# Revit family: ESTS
name_source: partatom
category: Mechanical Equipment
revit_build: Autodesk Revit 2018 (Build: 20170223_1515(x64)
units: mm (PartAtom-declared; Revit-internal decimal feet)

## family parameters
Always vertical = Yes
Cut with Voids When Loaded = No
Part Type = Normal
Room Calculation Point = No
Round Connector Dimension = Use Radius
Shared = No
Work Plane-Based = No

## types (92) — shared parameters
Description = Series Fan Powered Air Terminal with ECM Motor
Discharge Offset = 3"
Filter = 1"
Induction Offset = 1 1/8"
Inlet S = 5 1/2"
Manufacturer = Anemostat
Model = ESTS
URL = http://www.anemostat.com

## per-type parameters (varying)
| type | Diameter | Discharge Height "Y" | Discharge Width "X" | Duct Inlet | ELBOW LEFT | ELBOW RIGHT | Height | Induction Width "C" | Inlet Offset | Inlet Right | Left | Length | Q5A | Q5B | Q5Q | Radius | Right | Width |
| ESTS 3/4-hp - 07R with S/ELBOW | 6 7/8" | 16" | 19" | 3" | No | Yes | 20" | 21" | 3" | Yes | No | 48" | 20" | 24" | 20" | 3 7/16" | Yes | 48" |
| ESTS 3/4-hp - 07L with S/ELBOW | 6 7/8" | 16" | 19" | 3" | Yes | No | 20" | 21" | 4" | No | Yes | 48" | 20" | 24" | 20" | 3 7/16" | No | 48" |
| ESTS 3/4-hp - 07L W/OUT S/ELBOW | 6 7/8" | 16" | 19" | 3" | No | No | 20" | 21" | 4" | No | Yes | 48" | 20" | 24" | 20" | 3 7/16" | No | 48" |
| ESTS 3/4-hp - 07R W/OUT S/ELBOW | 6 7/8" | 16" | 19" | 3" | No | No | 20" | 21" | 3" | Yes | No | 48" | 20" | 24" | 20" | 3 7/16" | Yes | 48" |
| ESTS 1/3-hp - 10L W/OUT S/ELBOW | 9 7/8" | 11" | 11 1/2" | 5" | No | No | 18" | 12" | 4" | No | Yes | 36" | 18" | 18" | 18" | 4 15/16" | No | 32" |
| ESTS 1/3-hp - 10L with S/ELBOW | 9 7/8" | 11" | 11 1/2" | 5" | Yes | No | 18" | 12" | 4" | No | Yes | 36" | 18" | 18" | 18" | 4 15/16" | No | 32" |
| ESTS 1/3-hp - 10R with S/ELBOW | 9 7/8" | 11" | 11 1/2" | 5" | No | Yes | 18" | 12" | 4" | Yes | No | 36" | 18" | 18" | 18" | 4 15/16" | Yes | 32" |
| ESTS 1/3-hp - 10R W/OUT S/ELBOW | 9 7/8" | 11" | 11 1/2" | 5" | No | No | 18" | 12" | 4" | Yes | No | 36" | 18" | 18" | 18" | 4 15/16" | Yes | 32" |
| ESTS 1/2-hp - 14L W/OUT S/ELBOW | 13 7/8" | 12" | 14" | 7" | No | No | 18" | 17" | 4" | No | Yes | 40" | 18" | 20" | 18" | 6 15/16" | No | 40" |
| ESTS 1/2-hp - 14L with S/ELBOW | 13 7/8" | 12" | 14" | 7" | Yes | No | 18" | 17" | 4" | No | Yes | 40" | 18" | 20" | 18" | 6 15/16" | No | 40" |
| ESTS 1/2-hp - 14R W/OUT S/ELBOW | 13 7/8" | 12" | 14" | 7" | No | No | 18" | 17" | 4" | Yes | No | 40" | 18" | 20" | 18" | 6 15/16" | Yes | 40" |
| ESTS 1/2-hp - 14R with S/ELBOW | 13 7/8" | 12" | 14" | 7" | No | Yes | 18" | 17" | 4" | Yes | No | 40" | 18" | 20" | 18" | 6 15/16" | Yes | 40" |
| ESTS 1-hp - 16L W/OUT S/ELBOW | 15 7/8" | 16" | 19" | 8" | No | No | 20" | 21" | 4" | No | Yes | 48" | 20" | 24" | 20" | 7 15/16" | No | 48" |
| ESTS 1-hp - 16R W/OUT S/ELBOW | 15 7/8" | 16" | 19" | 8" | No | No | 20" | 21" | 4" | Yes | No | 48" | 20" | 24" | 20" | 7 15/16" | Yes | 48" |
| ESTS 1-hp - 16L with S/ELBOW | 15 7/8" | 16" | 19" | 8" | Yes | No | 20" | 21" | 4" | No | Yes | 48" | 20" | 24" | 20" | 7 15/16" | No | 48" |
| ESTS 1-hp - 16R with S/ELBOW | 15 7/8" | 16" | 19" | 8" | No | Yes | 20" | 21" | 4" | Yes | No | 48" | 20" | 24" | 20" | 7 15/16" | Yes | 48" |
| ESTS 1/2-hp - 12L W/OUT S/ELBOW | 11 7/8" | 12" | 14" | 6" | No | No | 18" | 17" | 4" | No | Yes | 40" | 18" | 20" | 18" | 5 15/16" | No | 40" |
| ESTS 1/2-hp - 12L with S/ELBOW | 11 7/8" | 12" | 14" | 6" | Yes | No | 18" | 17" | 4" | No | Yes | 40" | 18" | 20" | 18" | 5 15/16" | No | 40" |
| ESTS 1/2-hp - 12R W/OUT S/ELBOW | 11 7/8" | 12" | 14" | 6" | No | No | 18" | 17" | 4" | Yes | No | 40" | 18" | 20" | 18" | 5 15/16" | Yes | 40" |
| ESTS 1/2-hp - 12R with S/ELBOW | 11 7/8" | 12" | 14" | 6" | No | Yes | 18" | 17" | 4" | Yes | No | 40" | 18" | 20" | 18" | 5 15/16" | Yes | 40" |
| ESTS 1/2-hp - 10L W/OUT S/ELBOW | 9 7/8" | 12" | 14" | 5" | No | No | 18" | 17" | 4" | No | Yes | 40" | 18" | 20" | 18" | 4 15/16" | No | 40" |
| ESTS 1/2-hp - 10L with S/ELBOW | 9 7/8" | 12" | 14" | 5" | Yes | No | 18" | 17" | 4" | No | Yes | 40" | 18" | 20" | 18" | 4 15/16" | No | 40" |
| ESTS 1/2-hp - 10R W/OUT S/ELBOW | 9 7/8" | 12" | 14" | 5" | No | No | 18" | 17" | 4" | Yes | No | 40" | 18" | 20" | 18" | 4 15/16" | Yes | 40" |
| ESTS 1/2-hp - 10R with S/ELBOW | 9 7/8" | 12" | 14" | 5" | No | Yes | 18" | 17" | 4" | Yes | No | 40" | 18" | 20" | 18" | 4 15/16" | Yes | 40" |
| ESTS 1/2-hp - 09L W/OUT S/ELBOW | 8 7/8" | 12" | 14" | 4" | No | No | 18" | 17" | 4" | No | Yes | 40" | 18" | 20" | 18" | 4 7/16" | No | 40" |
| ESTS 1/2-hp - 09L with S/ELBOW | 8 7/8" | 12" | 14" | 4" | Yes | No | 18" | 17" | 4" | No | Yes | 40" | 18" | 20" | 18" | 4 7/16" | No | 40" |
| ESTS 1/2-hp - 09R W/OUT S/ELBOW | 8 7/8" | 12" | 14" | 4" | No | No | 18" | 17" | 4" | Yes | No | 40" | 18" | 20" | 18" | 4 7/16" | Yes | 40" |
| ESTS 1/2-hp - 09R with S/ELBOW | 8 7/8" | 12" | 14" | 4" | No | Yes | 18" | 17" | 4" | Yes | No | 40" | 18" | 20" | 18" | 4 7/16" | Yes | 40" |
| ESTS 1/2-hp - 08L W/OUT S/ELBOW | 7 7/8" | 12" | 14" | 4" | No | No | 18" | 17" | 4" | No | Yes | 40" | 18" | 20" | 18" | 3 15/16" | No | 40" |
| ESTS 1/2-hp - 08L with S/ELBOW | 7 7/8" | 12" | 14" | 4" | Yes | No | 18" | 17" | 4" | No | Yes | 40" | 18" | 20" | 18" | 3 15/16" | No | 40" |
| ESTS 1/2-hp - 08R W/OUT S/ELBOW | 7 7/8" | 12" | 14" | 4" | No | No | 18" | 17" | 4" | Yes | No | 40" | 18" | 20" | 18" | 3 15/16" | Yes | 40" |
| ESTS 1/2-hp - 08R with S/ELBOW | 7 7/8" | 12" | 14" | 4" | No | Yes | 18" | 17" | 4" | Yes | No | 40" | 18" | 20" | 18" | 3 15/16" | Yes | 40" |
| ESTS 1/2-hp - 07L W/OUT S/ELBOW | 6 7/8" | 12" | 14" | 3" | No | No | 18" | 17" | 4" | No | Yes | 40" | 18" | 20" | 18" | 3 7/16" | No | 40" |
| ESTS 1/2-hp - 07L with S/ELBOW | 6 7/8" | 12" | 14" | 3" | Yes | No | 18" | 17" | 4" | No | Yes | 40" | 18" | 20" | 18" | 3 7/16" | No | 40" |
| ESTS 1/2-hp - 07R W/OUT S/ELBOW | 6 7/8" | 12" | 14" | 3" | No | No | 18" | 17" | 4" | Yes | No | 40" | 18" | 20" | 18" | 3 7/16" | Yes | 40" |
| ESTS 1/2-hp - 07R with S/ELBOW | 6 7/8" | 12" | 14" | 3" | No | Yes | 18" | 17" | 4" | Yes | No | 40" | 18" | 20" | 18" | 3 7/16" | Yes | 40" |
| ESTS 1/2-hp - 06L W/OUT S/ELBOW | 5 7/8" | 12" | 14" | 3" | No | No | 18" | 17" | 4" | No | Yes | 40" | 18" | 20" | 18" | 2 15/16" | No | 40" |
| ESTS 1/2-hp - 06L with S/ELBOW | 5 7/8" | 12" | 14" | 3" | Yes | No | 18" | 17" | 4" | No | Yes | 40" | 18" | 20" | 18" | 2 15/16" | No | 40" |
| ESTS 1/2-hp - 06R W/OUT S/ELBOW | 5 7/8" | 12" | 14" | 3" | No | No | 18" | 17" | 4" | Yes | No | 40" | 18" | 20" | 18" | 2 15/16" | Yes | 40" |
| ESTS 1/2-hp - 06R with S/ELBOW | 5 7/8" | 12" | 14" | 3" | No | Yes | 18" | 17" | 4" | Yes | No | 40" | 18" | 20" | 18" | 2 15/16" | Yes | 40" |
| ESTS 1/3-hp - 09L W/OUT S/ELBOW | 8 7/8" | 11" | 11 1/2" | 4" | No | No | 18" | 12" | 4" | No | Yes | 36" | 18" | 18" | 18" | 4 7/16" | No | 32" |
| ESTS 1/3-hp - 09L with S/ELBOW | 8 7/8" | 11" | 11 1/2" | 4" | Yes | No | 18" | 12" | 4" | No | Yes | 36" | 18" | 18" | 18" | 4 7/16" | No | 32" |
| ESTS 1/3-hp - 09R W/OUT S/ELBOW | 8 7/8" | 11" | 11 1/2" | 4" | No | No | 18" | 12" | 4" | Yes | No | 36" | 18" | 18" | 18" | 4 7/16" | Yes | 32" |
| ESTS 1/3-hp - 09R with S/ELBOW | 8 7/8" | 11" | 11 1/2" | 4" | No | Yes | 18" | 12" | 4" | Yes | No | 36" | 18" | 18" | 18" | 4 7/16" | Yes | 32" |
| ESTS 1/3-hp - 08L W/OUT S/ELBOW | 7 7/8" | 11" | 11 1/2" | 4" | No | No | 18" | 12" | 4" | No | Yes | 36" | 18" | 18" | 18" | 3 15/16" | No | 32" |
| ESTS 1/3-hp - 08L with S/ELBOW | 7 7/8" | 11" | 11 1/2" | 4" | Yes | No | 18" | 12" | 4" | No | Yes | 36" | 18" | 18" | 18" | 3 15/16" | No | 32" |
| ESTS 1/3-hp - 08R W/OUT S/ELBOW | 7 7/8" | 11" | 11 1/2" | 4" | No | No | 18" | 12" | 4" | Yes | No | 36" | 18" | 18" | 18" | 3 15/16" | Yes | 32" |
| ESTS 1/3-hp - 08R with S/ELBOW | 7 7/8" | 11" | 11 1/2" | 4" | No | Yes | 18" | 12" | 4" | Yes | No | 36" | 18" | 18" | 18" | 3 15/16" | Yes | 32" |
| ESTS 1/3-hp - 07L W/OUT S/ELBOW | 6 7/8" | 11" | 11 1/2" | 3" | No | No | 18" | 12" | 4" | No | Yes | 36" | 18" | 18" | 18" | 3 7/16" | No | 32" |
| ESTS 1/3-hp - 07L with S/ELBOW | 6 7/8" | 11" | 11 1/2" | 3" | Yes | No | 18" | 12" | 4" | No | Yes | 36" | 18" | 18" | 18" | 3 7/16" | No | 32" |
| ESTS 1/3-hp - 07R W/OUT S/ELBOW | 6 7/8" | 11" | 11 1/2" | 3" | No | No | 18" | 12" | 4" | Yes | No | 36" | 18" | 18" | 18" | 3 7/16" | Yes | 32" |
| ESTS 1/3-hp - 07R with S/ELBOW | 6 7/8" | 11" | 11 1/2" | 3" | No | Yes | 18" | 12" | 4" | Yes | No | 36" | 18" | 18" | 18" | 3 7/16" | Yes | 32" |
| ESTS 1/3-hp - 06L W/OUT S/ELBOW | 5 7/8" | 11" | 11 1/2" | 3" | No | No | 18" | 12" | 4" | No | Yes | 36" | 18" | 18" | 18" | 2 15/16" | No | 32" |
| ESTS 1/3-hp - 06L with S/ELBOW | 5 7/8" | 11" | 11 1/2" | 3" | Yes | No | 18" | 12" | 4" | No | Yes | 36" | 18" | 18" | 18" | 2 15/16" | No | 32" |
| ESTS 1/3-hp - 06R W/OUT S/ELBOW | 5 7/8" | 11" | 11 1/2" | 3" | No | No | 18" | 12" | 4" | Yes | No | 36" | 18" | 18" | 18" | 2 15/16" | Yes | 32" |
| ESTS 1/3-hp - 06R with S/ELBOW | 5 7/8" | 11" | 11 1/2" | 3" | No | Yes | 18" | 12" | 4" | Yes | No | 36" | 18" | 18" | 18" | 2 15/16" | Yes | 32" |
| ESTS 1-hp - 14L W/OUT S/ELBOW | 13 7/8" | 16" | 19" | 7" | No | No | 20" | 21" | 4" | No | Yes | 48" | 20" | 24" | 20" | 6 15/16" | No | 48" |
| ESTS 1-hp - 14L with S/ELBOW | 13 7/8" | 16" | 19" | 7" | Yes | No | 20" | 21" | 4" | No | Yes | 48" | 20" | 24" | 20" | 6 15/16" | No | 48" |
| ESTS 1-hp - 14R W/OUT S/ELBOW | 13 7/8" | 16" | 19" | 7" | No | No | 20" | 21" | 4" | Yes | No | 48" | 20" | 24" | 20" | 6 15/16" | Yes | 48" |
| ESTS 1-hp - 14R with S/ELBOW | 13 7/8" | 16" | 19" | 7" | No | Yes | 20" | 21" | 4" | Yes | No | 48" | 20" | 24" | 20" | 6 15/16" | Yes | 48" |
| ESTS 1-hp - 12L W/OUT S/ELBOW | 11 7/8" | 16" | 19" | 6" | No | No | 20" | 21" | 4" | No | Yes | 48" | 20" | 24" | 20" | 5 15/16" | No | 48" |
| ESTS 1-hp - 12L with S/ELBOW | 11 7/8" | 16" | 19" | 6" | Yes | No | 20" | 21" | 4" | No | Yes | 48" | 20" | 24" | 20" | 5 15/16" | No | 48" |
| ESTS 1-hp - 12R W/OUT S/ELBOW | 11 7/8" | 16" | 19" | 6" | No | No | 20" | 21" | 4" | Yes | No | 48" | 20" | 24" | 20" | 5 15/16" | Yes | 48" |
| ESTS 1-hp - 12R with S/ELBOW | 11 7/8" | 16" | 19" | 6" | No | Yes | 20" | 21" | 4" | Yes | No | 48" | 20" | 24" | 20" | 5 15/16" | Yes | 48" |
| ESTS 1-hp - 10L W/OUT S/ELBOW | 9 7/8" | 16" | 19" | 5" | No | No | 20" | 21" | 4" | No | Yes | 48" | 20" | 24" | 20" | 4 15/16" | No | 48" |
| ESTS 1-hp - 10L with S/ELBOW | 9 7/8" | 16" | 19" | 5" | Yes | No | 20" | 21" | 4" | No | Yes | 48" | 20" | 24" | 20" | 4 15/16" | No | 48" |
| ESTS 1-hp - 10R W/OUT S/ELBOW | 9 7/8" | 16" | 19" | 5" | No | No | 20" | 21" | 4" | Yes | No | 48" | 20" | 24" | 20" | 4 15/16" | Yes | 48" |
| ESTS 1-hp - 10R with S/ELBOW | 9 7/8" | 16" | 19" | 5" | No | Yes | 20" | 21" | 4" | Yes | No | 48" | 20" | 24" | 20" | 4 15/16" | Yes | 48" |
| ESTS 1-hp - 09L W/OUT S/ELBOW | 8 7/8" | 16" | 19" | 4" | No | No | 20" | 21" | 4" | No | Yes | 48" | 20" | 24" | 20" | 4 7/16" | No | 48" |
| ESTS 1-hp - 09L with S/ELBOW | 8 7/8" | 16" | 19" | 4" | Yes | No | 20" | 21" | 4" | No | Yes | 48" | 20" | 24" | 20" | 4 7/16" | No | 48" |
| ESTS 1-hp - 09R W/OUT S/ELBOW | 8 7/8" | 16" | 19" | 4" | No | No | 20" | 21" | 4" | Yes | No | 48" | 20" | 24" | 20" | 4 7/16" | Yes | 48" |
| ESTS 1-hp - 09R with S/ELBOW | 8 7/8" | 16" | 19" | 4" | No | Yes | 20" | 21" | 4" | Yes | No | 48" | 20" | 24" | 20" | 4 7/16" | Yes | 48" |
| ESTS 3/4-hp - 08L W/OUT S/ELBOW | 7 7/8" | 16" | 19" | 4" | No | No | 20" | 21" | 4" | No | Yes | 48" | 20" | 24" | 20" | 3 15/16" | No | 48" |
| ESTS 3/4-hp - 08L with S/ELBOW | 7 7/8" | 16" | 19" | 4" | Yes | No | 20" | 21" | 4" | No | Yes | 48" | 20" | 24" | 20" | 3 15/16" | No | 48" |
| ESTS 3/4-hp - 08R W/OUT S/ELBOW | 7 7/8" | 16" | 19" | 4" | No | No | 20" | 21" | 3" | Yes | No | 48" | 20" | 24" | 20" | 3 15/16" | Yes | 48" |
| ESTS 3/4-hp - 08R with S/ELBOW | 7 7/8" | 16" | 19" | 4" | No | Yes | 20" | 21" | 3" | Yes | No | 48" | 20" | 24" | 20" | 3 15/16" | Yes | 48" |
| ESTS 3/4-hp - 09L W/OUT S/ELBOW | 8 7/8" | 16" | 19" | 4" | No | No | 20" | 21" | 4" | No | Yes | 48" | 20" | 24" | 20" | 4 7/16" | No | 48" |
| ESTS 3/4-hp - 09L with S/ELBOW | 8 7/8" | 16" | 19" | 4" | Yes | No | 20" | 21" | 4" | No | Yes | 48" | 20" | 24" | 20" | 4 7/16" | No | 48" |
| ESTS 3/4-hp - 09R W/OUT S/ELBOW | 8 7/8" | 16" | 19" | 4" | No | No | 20" | 21" | 3" | Yes | No | 48" | 20" | 24" | 20" | 4 7/16" | Yes | 48" |
| ESTS 3/4-hp - 09R with S/ELBOW | 8 7/8" | 16" | 19" | 4" | No | Yes | 20" | 21" | 3" | Yes | No | 48" | 20" | 24" | 20" | 4 7/16" | Yes | 48" |
| ESTS 3/4-hp - 10L W/OUT S/ELBOW | 9 7/8" | 16" | 19" | 5" | No | No | 20" | 21" | 4" | No | Yes | 48" | 20" | 24" | 20" | 4 15/16" | No | 48" |
| ESTS 3/4-hp - 10L with S/ELBOW | 9 7/8" | 16" | 19" | 5" | Yes | No | 20" | 21" | 4" | No | Yes | 48" | 20" | 24" | 20" | 4 15/16" | No | 48" |
| ESTS 3/4-hp - 10R W/OUT S/ELBOW | 9 7/8" | 16" | 19" | 5" | No | No | 20" | 21" | 3" | Yes | No | 48" | 20" | 24" | 20" | 4 15/16" | Yes | 48" |
| ESTS 3/4-hp - 10R with S/ELBOW | 9 7/8" | 16" | 19" | 5" | No | Yes | 20" | 21" | 3" | Yes | No | 48" | 20" | 24" | 20" | 4 15/16" | Yes | 48" |
| ESTS 3/4-hp - 12L W/OUT S/ELBOW | 11 7/8" | 16" | 19" | 6" | No | No | 20" | 21" | 4" | No | Yes | 48" | 20" | 24" | 20" | 5 15/16" | No | 48" |
| ESTS 3/4-hp - 12L with S/ELBOW | 11 7/8" | 16" | 19" | 6" | Yes | No | 20" | 21" | 4" | No | Yes | 48" | 20" | 24" | 20" | 5 15/16" | No | 48" |
| ESTS 3/4-hp - 12R W/OUT S/ELBOW | 11 7/8" | 16" | 19" | 6" | No | No | 20" | 21" | 3" | Yes | No | 48" | 20" | 24" | 20" | 5 15/16" | Yes | 48" |
| ESTS 3/4-hp - 12R with S/ELBOW | 11 7/8" | 16" | 19" | 6" | No | Yes | 20" | 21" | 3" | Yes | No | 48" | 20" | 24" | 20" | 5 15/16" | Yes | 48" |
| ESTS 3/4-hp - 14L W/OUT S/ELBOW | 13 7/8" | 16" | 19" | 7" | No | No | 20" | 21" | 4" | No | Yes | 48" | 20" | 24" | 20" | 6 15/16" | No | 48" |
| ESTS 3/4-hp - 14L with S/ELBOW | 13 7/8" | 16" | 19" | 7" | Yes | No | 20" | 21" | 4" | No | Yes | 48" | 20" | 24" | 20" | 6 15/16" | No | 48" |
| ESTS 3/4-hp - 14R W/OUT S/ELBOW | 13 7/8" | 16" | 19" | 7" | No | No | 20" | 21" | 3" | Yes | No | 48" | 20" | 24" | 20" | 6 15/16" | Yes | 48" |
| ESTS 3/4-hp - 14R with S/ELBOW | 13 7/8" | 16" | 19" | 7" | No | Yes | 20" | 21" | 3" | Yes | No | 48" | 20" | 24" | 20" | 6 15/16" | Yes | 48" |

## geometry (parser evidence)
native form markers: Sweep x1
no freeform markers — native parametric forms only
